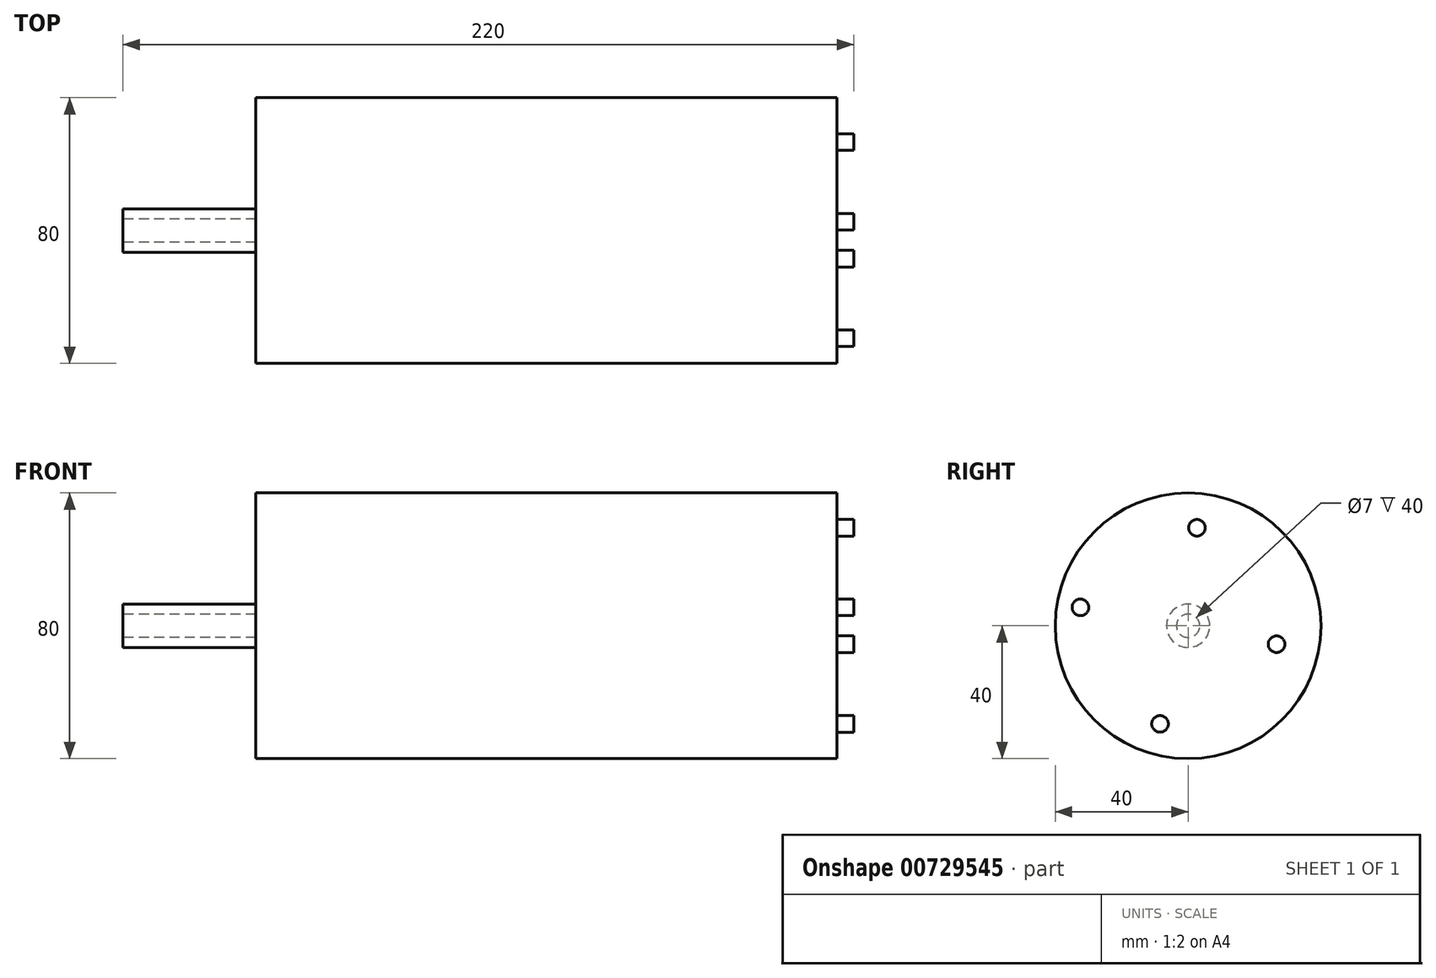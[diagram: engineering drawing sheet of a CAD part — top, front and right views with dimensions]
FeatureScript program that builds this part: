
annotation { "Feature Type Name" : "Feature", "Feature Type Description" : "" }
export const myFeature = defineFeature(function(context is Context, id is Id, definition is map)
    precondition{}
    {
        {
            var Q0;
            Q0=qCreatedBy(makeId("Front.planeOp"),FACE);
            var sketch = newSketch(context, id + "F0", { "sketchPlane" : qUnion([Q0])});
            skLineSegment(sketch, "E0", {"start": v(-122.68, 0) * mm, "end": v(160.18, 0) * mm});
            skLineSegment(sketch, "E1.bottom", {"start": v(-14.82, 40) * mm, "end": v(160.18, 40) * mm});
            skLineSegment(sketch, "E1.top", {"start": v(-14.82, -40) * mm, "end": v(160.18, -40) * mm});
            skLineSegment(sketch, "E1.left", {"start": v(-14.82, 40) * mm, "end": v(-14.82, -40) * mm});
            skLineSegment(sketch, "E1.right", {"start": v(160.18, 40) * mm, "end": v(160.18, -40) * mm});
            skPoint(sketch, "E1.middle", {"position": v(72.68, 0) * mm});
            skLineSegment(sketch, "E2.bottom", {"start": v(-14.82, 6.5) * mm, "end": v(-54.82, 6.5) * mm});
            skLineSegment(sketch, "E2.top", {"start": v(-14.82, -6.5) * mm, "end": v(-54.82, -6.5) * mm});
            skLineSegment(sketch, "E2.left", {"start": v(-14.82, 6.5) * mm, "end": v(-14.82, -6.5) * mm});
            skLineSegment(sketch, "E2.right", {"start": v(-54.82, 6.5) * mm, "end": v(-54.82, 0) * mm});
            skPoint(sketch, "E2.middle", {"position": v(-34.82, 0) * mm});
            skLineSegment(sketch, "E3.bottom", {"start": v(-14.82, 3.5) * mm, "end": v(-54.82, 3.5) * mm});
            skLineSegment(sketch, "E3.top", {"start": v(-14.82, -3.5) * mm, "end": v(-54.82, -3.5) * mm});
            skLineSegment(sketch, "E3.left", {"start": v(-14.82, 3.5) * mm, "end": v(-14.82, 0) * mm});
            skLineSegment(sketch, "E3.right", {"start": v(-54.82, 3.5) * mm, "end": v(-54.82, 0) * mm});
            skLineSegment(sketch, "E4", {"start": v(-54.82, 0) * mm, "end": v(-54.82, -6.5) * mm});
            skLineSegment(sketch, "E5", {"start": v(-54.82, 0) * mm, "end": v(-54.82, -3.5) * mm});
            skLineSegment(sketch, "E6", {"start": v(-14.82, 0) * mm, "end": v(-14.82, -3.5) * mm});
            skSolve(sketch);
        }
        {
            var Q0;
            {var subQ2=sQuery(id+"F0.wireOp",EDGE,"E2.bottom");Q0=makeQuery(id+"F0.imprint","IMPRINT",FACE,{"disambiguationData":[TD([[makeQuery(id+"F0.imprint","IMPRINT",EDGE,{"derivedFrom":subQ2}),1.0]])]});}
            var Q1;
            {var subQ4=sQuery(id+"F0.wireOp",EDGE,"E1.bottom");Q1=makeQuery(id+"F0.imprint","IMPRINT",FACE,{"disambiguationData":[TD([[makeQuery(id+"F0.imprint","IMPRINT",EDGE,{"derivedFrom":subQ4}),-1.0]])]});}
            var Q2;
            Q2=sQuery(id+"F0.wireOp",EDGE,"E0");
            revolve(context, id + "F1", {"surfaceOperationType" : NewSurfaceOperationType.NEW, "entities" : qUnion([Q0, Q1]), "axis" : qUnion([Q2]), "revolveType" : RevolveType.FULL});
        }
        {
            var Q0;
            Q0=makeQuery(id+"F1.opRevolve","SWEPT_FACE",FACE,{"disambiguationData":[OSD([sQuery(id+"F0.wireOp",EDGE,"E1.right")])]});
            var sketch = newSketch(context, id + "F2", { "sketchPlane" : qUnion([Q0])});
            skCircle(sketch, "E7", {"center": v(-8.45, -29.52) * mm, "radius": 2.5 * mm});
            skCircle(sketch, "E8.1.0", {"center": v(26.62, -5.55) * mm, "radius": 2.5 * mm});
            skCircle(sketch, "E8.2.0", {"center": v(2.65, 29.52) * mm, "radius": 2.5 * mm});
            skCircle(sketch, "E8.3.0", {"center": v(-32.42, 5.55) * mm, "radius": 2.5 * mm});
            skPoint(sketch, "E8.center", {"position": v(-2.9, 0) * mm});
            skSolve(sketch);
        }
        {
            var Q0;
            Q0=makeQuery(id+"F2.imprint","IMPRINT",FACE,{"disambiguationData":[TD([[makeQuery(id+"F2.imprint","IMPRINT",EDGE,{"derivedFrom":sQuery(id+"F2.wireOp",EDGE,"E8.2.0")}),1.0]])]});
            var Q1;
            Q1=makeQuery(id+"F2.imprint","IMPRINT",FACE,{"disambiguationData":[TD([[makeQuery(id+"F2.imprint","IMPRINT",EDGE,{"derivedFrom":sQuery(id+"F2.wireOp",EDGE,"E7")}),1.0]])]});
            var Q2;
            Q2=makeQuery(id+"F2.imprint","IMPRINT",FACE,{"disambiguationData":[TD([[makeQuery(id+"F2.imprint","IMPRINT",EDGE,{"derivedFrom":sQuery(id+"F2.wireOp",EDGE,"E8.1.0")}),1.0]])]});
            var Q3;
            Q3=makeQuery(id+"F2.imprint","IMPRINT",FACE,{"disambiguationData":[TD([[makeQuery(id+"F2.imprint","IMPRINT",EDGE,{"derivedFrom":sQuery(id+"F2.wireOp",EDGE,"E8.3.0")}),1.0]])]});
            extrude(context, id + "F3", {"entities" : qUnion([Q0, Q1, Q2, Q3]), "operationType" : NewBodyOperationType.ADD, "depth" : 5 * mm, "offsetDistance" : 25 * mm});
        }
    });
